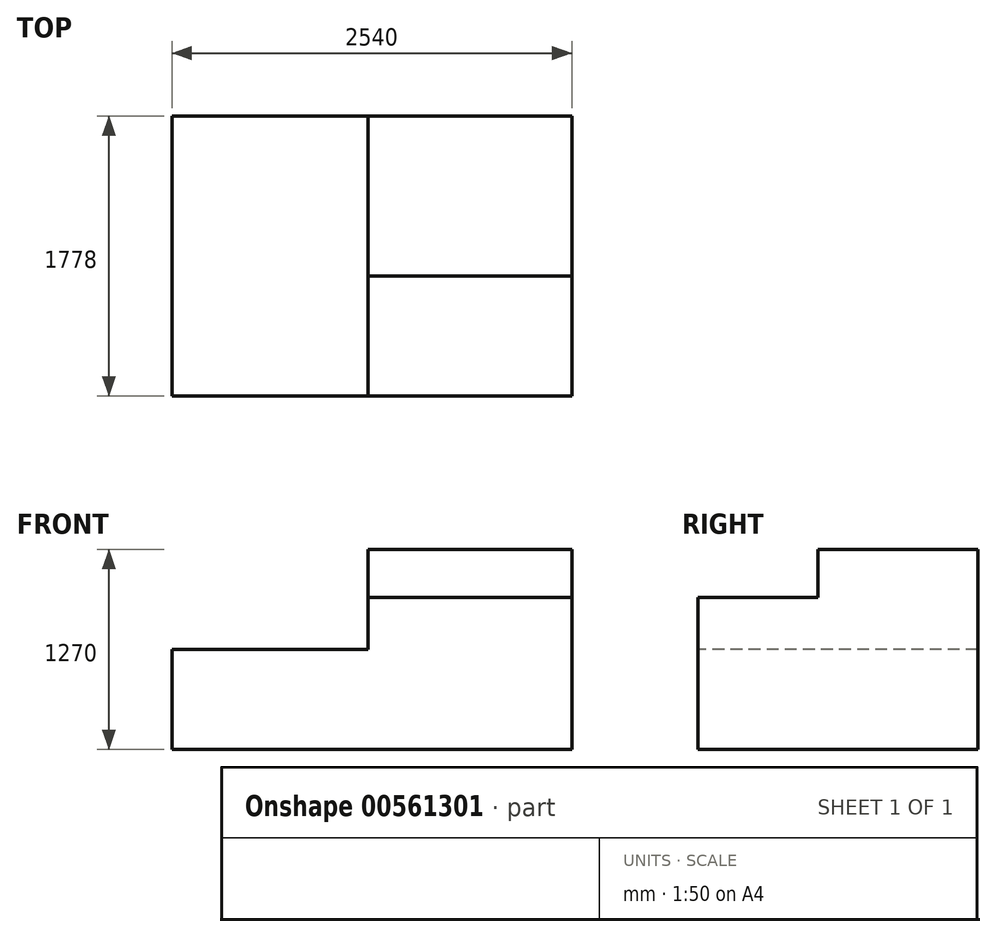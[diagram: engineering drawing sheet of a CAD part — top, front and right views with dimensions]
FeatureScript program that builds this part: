
annotation { "Feature Type Name" : "Feature", "Feature Type Description" : "" }
export const myFeature = defineFeature(function(context is Context, id is Id, definition is map)
    precondition{}
    {
        {
            var Q0;
            Q0=qCreatedBy(makeId("Front.planeOp"),FACE);
            var sketch = newSketch(context, id + "F0", { "sketchPlane" : qUnion([Q0])});
            skLineSegment(sketch, "E0.bottom", {"start": v(1270, 635) * mm, "end": v(-1270, 635) * mm});
            skLineSegment(sketch, "E0.top", {"start": v(1270, -635) * mm, "end": v(-1270, -635) * mm});
            skLineSegment(sketch, "E0.left", {"start": v(1270, 635) * mm, "end": v(1270, -635) * mm});
            skLineSegment(sketch, "E0.right", {"start": v(-1270, 635) * mm, "end": v(-1270, -635) * mm});
            skPoint(sketch, "E0.middle", {"position": v(0, 0) * mm});
            skSolve(sketch);
        }
        {
            var Q0;
            Q0 = qSketchRegion(id + "F0", true);
            extrude(context, id + "F1", {"entities" : qUnion([Q0]), "depth" : 1778 * mm, "offsetDistance" : 25.4 * mm});
        }
        {
            var Q0;
            Q0=makeQuery(id+"F1.opExtrude","CAP_FACE",FACE,{"disambiguationData":[OSD([sQuery(id+"F0.wireOp",EDGE,"E0.bottom"),sQuery(id+"F0.wireOp",EDGE,"E0.top"),sQuery(id+"F0.wireOp",EDGE,"E0.left"),sQuery(id+"F0.wireOp",EDGE,"E0.right")])],"isStart":false});
            var sketch = newSketch(context, id + "F2", { "sketchPlane" : qUnion([Q0])});
            skLineSegment(sketch, "E1.bottom", {"start": v(0, 0) * mm, "end": v(-1270, 0) * mm});
            skLineSegment(sketch, "E1.top", {"start": v(0, 635) * mm, "end": v(-1270, 635) * mm});
            skLineSegment(sketch, "E1.left", {"start": v(0, 0) * mm, "end": v(0, 635) * mm});
            skLineSegment(sketch, "E1.right", {"start": v(-1270, 0) * mm, "end": v(-1270, 635) * mm});
            skSolve(sketch);
        }
        {
            var Q0;
            Q0 = qSketchRegion(id + "F2", true);
            extrude(context, id + "F3", {"entities" : qUnion([Q0]), "operationType" : NewBodyOperationType.REMOVE, "endBound" : BoundingType.THROUGH_ALL, "oppositeDirection" : true, "depth" : 25.4 * mm, "offsetDistance" : 25.4 * mm});
        }
        {
            var Q0;
            Q0=makeQuery(id+"F3.boolean.opBoolean","COPY",FACE,{"derivedFrom":makeQuery(id+"F3.opExtrude","SWEPT_FACE",FACE,{"disambiguationData":[OSD([sQuery(id+"F2.wireOp",EDGE,"E1.left")])]})});
            extrude(context, id + "F4", {"entities" : qUnion([Q0]), "operationType" : NewBodyOperationType.ADD, "depth" : 25.4 * mm, "offsetDistance" : 25.4 * mm});
        }
        {
            var Q0;
            Q0=makeQuery(id+"F4.opExtrude","CAP_FACE",FACE,{"disambiguationData":[OSD([sQuery(id+"F2.wireOp",EDGE,"E1.left")])],"isStart":false});
            var sketch = newSketch(context, id + "F5", { "sketchPlane" : qUnion([Q0])});
            skLineSegment(sketch, "E2.bottom", {"start": v(1778, 635) * mm, "end": v(1016, 635) * mm});
            skLineSegment(sketch, "E2.top", {"start": v(1778, 330.2) * mm, "end": v(1016, 330.2) * mm});
            skLineSegment(sketch, "E2.left", {"start": v(1778, 635) * mm, "end": v(1778, 330.2) * mm});
            skLineSegment(sketch, "E2.right", {"start": v(1016, 635) * mm, "end": v(1016, 330.2) * mm});
            skSolve(sketch);
        }
        {
            var Q0;
            Q0 = qSketchRegion(id + "F5", true);
            extrude(context, id + "F6", {"entities" : qUnion([Q0]), "operationType" : NewBodyOperationType.REMOVE, "endBound" : BoundingType.THROUGH_ALL, "oppositeDirection" : true, "depth" : 25.4 * mm, "offsetDistance" : 25.4 * mm});
        }
    });
